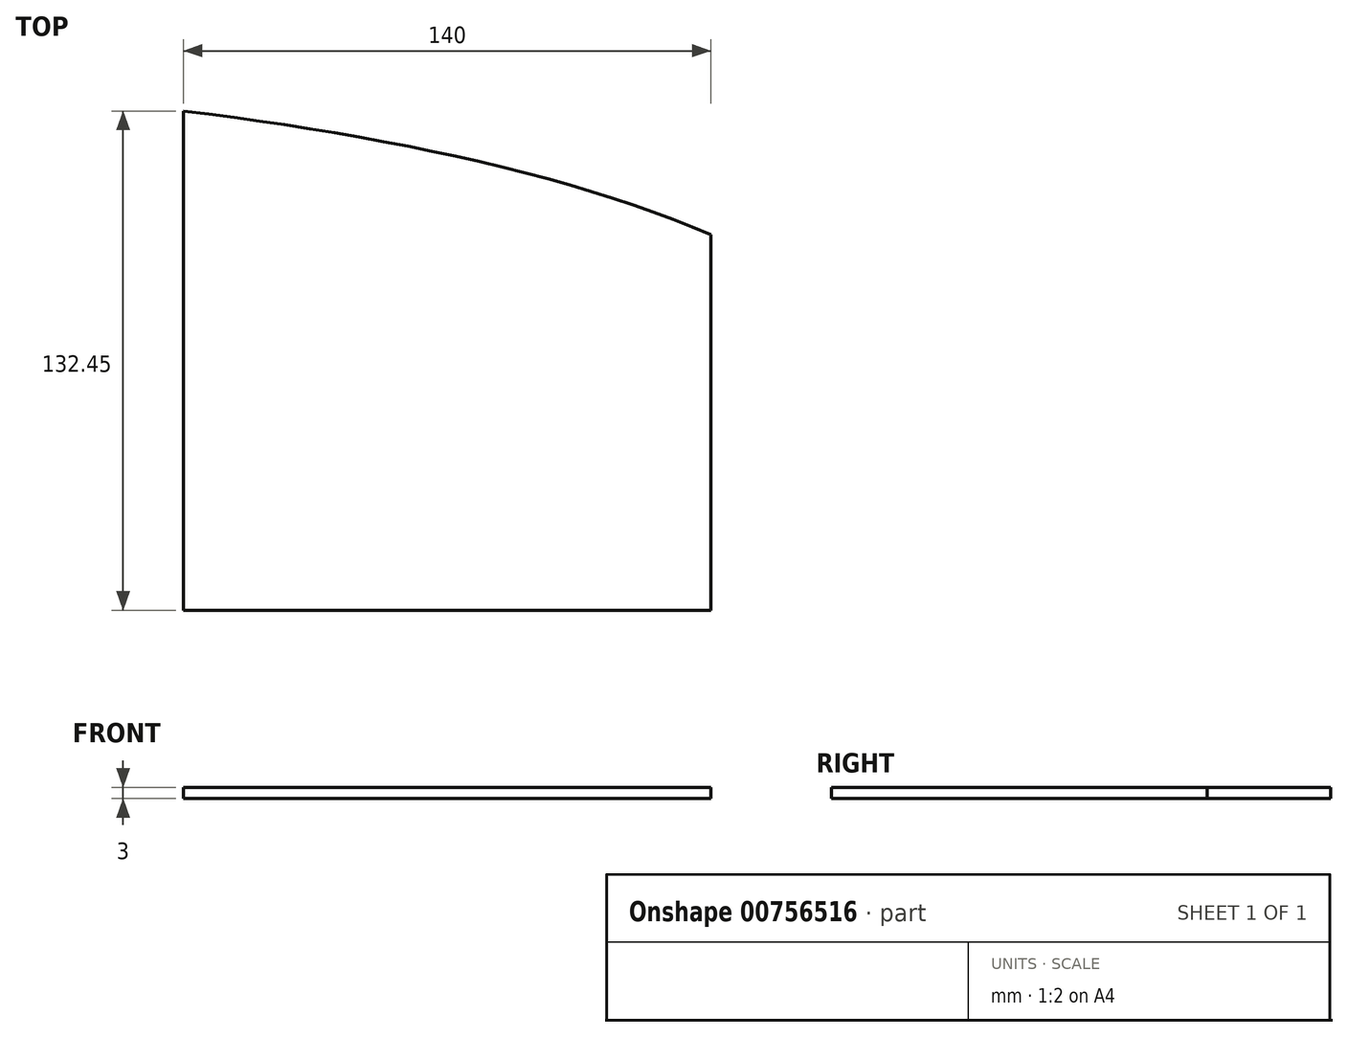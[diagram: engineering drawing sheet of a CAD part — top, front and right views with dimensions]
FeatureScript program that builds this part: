
annotation { "Feature Type Name" : "Feature", "Feature Type Description" : "" }
export const myFeature = defineFeature(function(context is Context, id is Id, definition is map)
    precondition{}
    {
        {
            var Q0;
            Q0=qCreatedBy(makeId("Top.planeOp"),FACE);
            var sketch = newSketch(context, id + "F0", { "sketchPlane" : qUnion([Q0])});
            skLineSegment(sketch, "E0.right", {"start": v(-155, -140) * mm, "end": v(-155, 140) * mm});
            skPoint(sketch, "E0.middle", {"position": v(0, 0) * mm});
            skLineSegment(sketch, "E1", {"start": v(165, 0) * mm, "end": v(165, 70) * mm});
            skLineSegment(sketch, "E2", {"start": v(165, 0) * mm, "end": v(165, -50) * mm});
            skLineSegment(sketch, "E3", {"start": v(165, 0) * mm, "end": v(185, 0) * mm});
            skLineSegment(sketch, "E4", {"start": v(-155, 140) * mm, "end": v(-155, -140) * mm});
            skFitSpline(sketch, "E5", {"points": [v(-155, 140) * mm, v(165, 70) * mm, v(185, 0) * mm], "startDerivative": vector(449.36, 4.91) * mm, "endDerivative": vector(26.44, -99.47) * mm});
            skLineSegment(sketch, "E6", {"start": v(165, 0) * mm, "end": v(-155, 0) * mm});
            skSolve(sketch);
        }
        {
            var Q0;
            Q0 = qSketchRegion(id + "F0", true);
            var Q1;
            {var subQ0=sQuery(id+"F0.wireOp",EDGE,"E1");Q1=makeQuery(id+"F0.imprint","IMPRINT",FACE,{"disambiguationData":[TD([[makeQuery(id+"F0.imprint","IMPRINT",EDGE,{"derivedFrom":subQ0}),1.0]])]});}
            extrude(context, id + "F1", {"entities" : qUnion([Q0, Q1]), "depth" : 3 * mm, "offsetDistance" : 25 * mm});
        }
        {
            var Q0;
            Q0=qCreatedBy(makeId("Top.planeOp"),FACE);
            var sketch = newSketch(context, id + "F2", { "sketchPlane" : qUnion([Q0])});
            skLineSegment(sketch, "E7.bottom", {"start": v(450, -150) * mm, "end": v(-450, -150) * mm});
            skLineSegment(sketch, "E7.top", {"start": v(450, 150) * mm, "end": v(-450, 150) * mm});
            skLineSegment(sketch, "E7.left", {"start": v(450, -150) * mm, "end": v(450, 150) * mm});
            skLineSegment(sketch, "E7.right", {"start": v(-450, -150) * mm, "end": v(-450, 150) * mm});
            skPoint(sketch, "E7.middle", {"position": v(0, 0) * mm});
            skLineSegment(sketch, "E8.bottom", {"start": v(70, -147.5) * mm, "end": v(-70, -147.5) * mm});
            skLineSegment(sketch, "E8.top", {"start": v(70, 147.5) * mm, "end": v(-70, 147.5) * mm});
            skLineSegment(sketch, "E8.left", {"start": v(70, -147.5) * mm, "end": v(70, 147.5) * mm});
            skLineSegment(sketch, "E8.right", {"start": v(-70, -147.5) * mm, "end": v(-70, 147.5) * mm});
            skSolve(sketch);
        }
        {
            var Q0;
            Q0 = qSketchRegion(id + "F2", true);
            extrude(context, id + "F3", {"entities" : qUnion([Q0]), "depth" : 25 * mm, "offsetDistance" : 25 * mm});
        }
        {
            var Q0;
            Q0=makeQuery(id+"F3.opExtrude","SWEPT_BODY",BODY,{"disambiguationData":[OSD([sQuery(id+"F2.wireOp",EDGE,"E7.bottom"),sQuery(id+"F2.wireOp",EDGE,"E7.top"),sQuery(id+"F2.wireOp",EDGE,"E7.left"),sQuery(id+"F2.wireOp",EDGE,"E7.right"),sQuery(id+"F2.wireOp",EDGE,"E8.bottom"),sQuery(id+"F2.wireOp",EDGE,"E8.top"),sQuery(id+"F2.wireOp",EDGE,"E8.left"),sQuery(id+"F2.wireOp",EDGE,"E8.right")])]});
            transform(context, id + "F4", {"entities" : qUnion([Q0]), "transformType" : TransformType.TRANSLATION_3D, "dx" : 50 * mm, "dy" : 0 * mm, "dz" : 0 * mm, "makeCopy" : false});
        }
        {
            var Q0;
            Q0=makeQuery(id+"F3.opExtrude","SWEPT_BODY",BODY,{"disambiguationData":[OSD([sQuery(id+"F2.wireOp",EDGE,"E7.bottom"),sQuery(id+"F2.wireOp",EDGE,"E7.top"),sQuery(id+"F2.wireOp",EDGE,"E7.left"),sQuery(id+"F2.wireOp",EDGE,"E7.right"),sQuery(id+"F2.wireOp",EDGE,"E8.bottom"),sQuery(id+"F2.wireOp",EDGE,"E8.top"),sQuery(id+"F2.wireOp",EDGE,"E8.left"),sQuery(id+"F2.wireOp",EDGE,"E8.right")])]});
            var Q1;
            Q1=makeQuery(id+"F1.opExtrude","SWEPT_BODY",BODY,{"disambiguationData":[OSD([sQuery(id+"F0.wireOp",EDGE,"E3"),sQuery(id+"F0.wireOp",EDGE,"E4"),sQuery(id+"F0.wireOp",EDGE,"E5"),sQuery(id+"F0.wireOp",EDGE,"9lJyaOmw-jQZn-ORA2-WQ9A-DhjmkDvq9OXz")])]});
            booleanBodies(context, id + "F5", {"operationType" : BooleanOperationType.SUBTRACTION, "tools" : qUnion([Q0]), "targets" : qUnion([Q1])});
        }
    });
